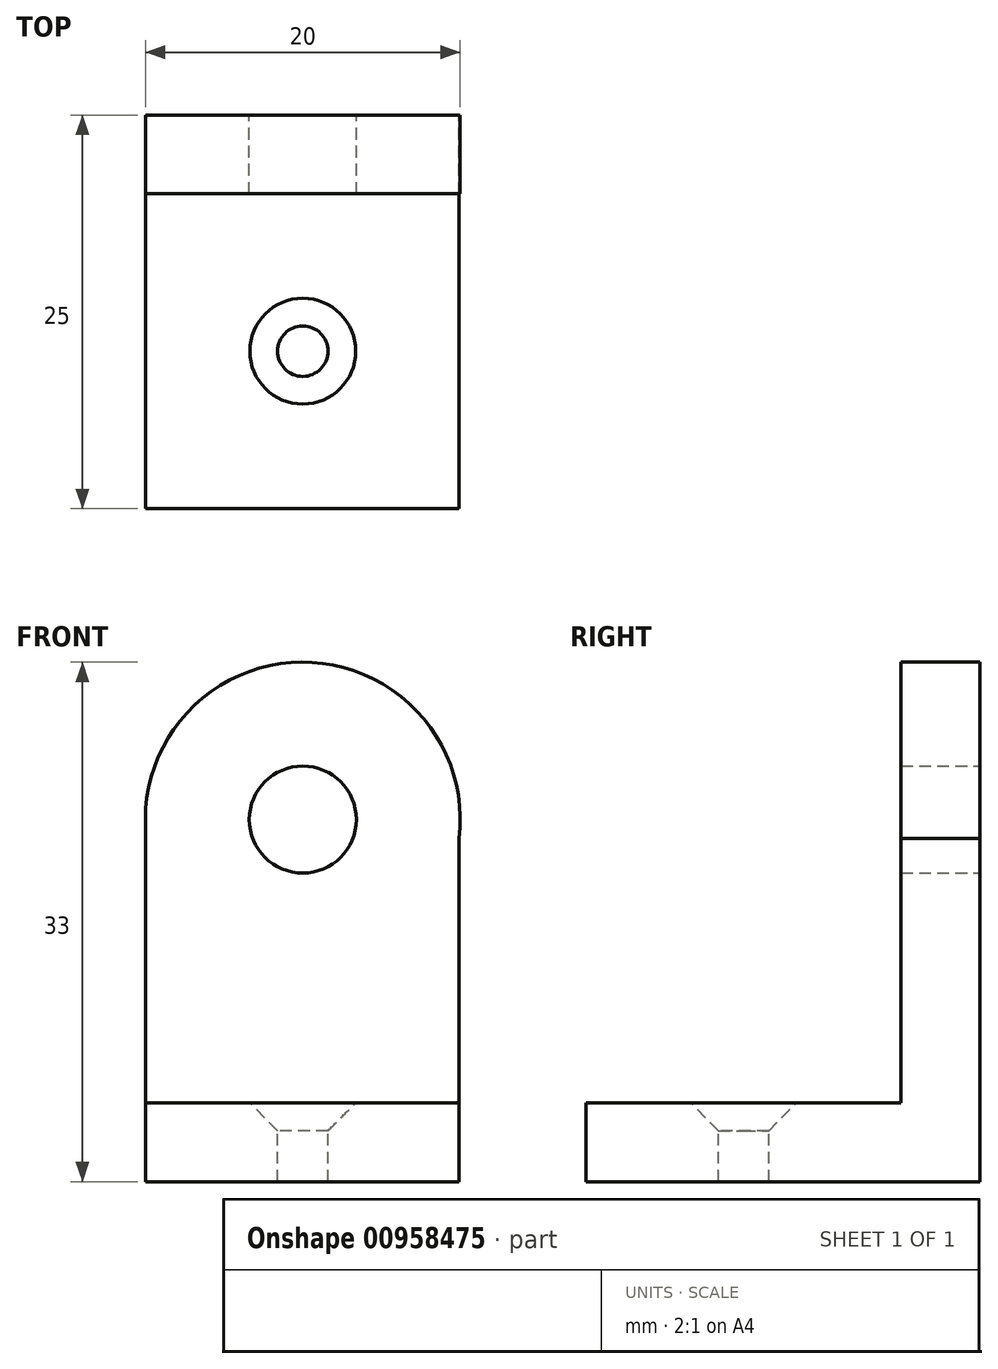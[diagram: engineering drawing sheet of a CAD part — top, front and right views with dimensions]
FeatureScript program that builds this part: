
annotation { "Feature Type Name" : "Feature", "Feature Type Description" : "" }
export const myFeature = defineFeature(function(context is Context, id is Id, definition is map)
    precondition{}
    {
        {
            var Q0;
            Q0=qCreatedBy(makeId("Front.planeOp"),FACE);
            var sketch = newSketch(context, id + "F0", { "sketchPlane" : qUnion([Q0])});
            skArc(sketch, "E0", {"start": v(9.93, -1.19) * mm, "mid": v(0.6, 9.98) * mm, "end": v(-10, 0) * mm});
            skLineSegment(sketch, "E1.top", {"start": v(-10, -23) * mm, "end": v(9.93, -23) * mm});
            skLineSegment(sketch, "E1.left", {"start": v(-10, 0) * mm, "end": v(-10, -23) * mm});
            skLineSegment(sketch, "E1.right", {"start": v(9.93, 0) * mm, "end": v(9.93, -23) * mm});
            skSolve(sketch);
        }
        {
            var Q0;
            {var subQ0=sQuery(id+"F0.wireOp",EDGE,"E0");Q0=makeQuery(id+"F0.imprint","IMPRINT",FACE,{"disambiguationData":[TD([[makeQuery(id+"F0.imprint","IMPRINT",EDGE,{"derivedFrom":subQ0}),1.0]])]});}
            extrude(context, id + "F1", {"entities" : qUnion([Q0]), "depth" : 5 * mm, "offsetDistance" : 25 * mm});
        }
        {
            var Q0;
            Q0=makeQuery(id+"F1.opExtrude","CAP_FACE",FACE,{"disambiguationData":[OSD([sQuery(id+"F0.wireOp",EDGE,"E0"),sQuery(id+"F0.wireOp",EDGE,"E1.top"),sQuery(id+"F0.wireOp",EDGE,"E1.left"),sQuery(id+"F0.wireOp",EDGE,"E1.right")])],"isStart":false});
            var sketch = newSketch(context, id + "F2", { "sketchPlane" : qUnion([Q0])});
            skLineSegment(sketch, "E2.bottom", {"start": v(-10, -23) * mm, "end": v(9.93, -23) * mm});
            skLineSegment(sketch, "E2.top", {"start": v(-10, -18) * mm, "end": v(9.93, -18) * mm});
            skLineSegment(sketch, "E2.left", {"start": v(-10, -23) * mm, "end": v(-10, -18) * mm});
            skLineSegment(sketch, "E2.right", {"start": v(9.93, -23) * mm, "end": v(9.93, -18) * mm});
            skSolve(sketch);
        }
        {
            var Q0;
            Q0=makeQuery(id+"F2.imprint","IMPRINT",FACE,{"disambiguationData":[TD([[makeQuery(id+"F2.imprint","IMPRINT",EDGE,{"derivedFrom":sQuery(id+"F2.wireOp",EDGE,"E2.bottom")}),1.0]])]});
            extrude(context, id + "F3", {"entities" : qUnion([Q0]), "operationType" : NewBodyOperationType.ADD, "depth" : 20 * mm, "offsetDistance" : 25 * mm});
        }
        {
            var Q0;
            Q0=makeQuery(id+"F1.opExtrude","CAP_FACE",FACE,{"disambiguationData":[OSD([sQuery(id+"F0.wireOp",EDGE,"E0"),sQuery(id+"F0.wireOp",EDGE,"E1.top"),sQuery(id+"F0.wireOp",EDGE,"E1.left"),sQuery(id+"F0.wireOp",EDGE,"E1.right")])],"isStart":true});
            var sketch = newSketch(context, id + "F4", { "sketchPlane" : qUnion([Q0])});
            skPoint(sketch, "E3", {"position": v(0, 0) * mm});
            skSolve(sketch);
        }
        {
            var Q0;
            Q0=sQuery(id+"F4.wireOp",VERTEX,"E3");
            var Q1;
            Q1=makeQuery(id+"F1.opExtrude","SWEPT_BODY",BODY,{"disambiguationData":[OSD([sQuery(id+"F0.wireOp",EDGE,"E0"),sQuery(id+"F0.wireOp",EDGE,"E1.top"),sQuery(id+"F0.wireOp",EDGE,"E1.left"),sQuery(id+"F0.wireOp",EDGE,"E1.right")])]});
            hole(context, id + "F5", {"style" : HoleStyle.SIMPLE, "endStyle" : HoleEndStyle.THROUGH, "standardTappedOrClearance" : lookupTablePath({ "standard" : "ISO", "engagement" : "75%", "pitch" : "1.25 mm", "size" : "M8", "type" : "Tapped" }), "standardBlindInLast" : lookupTablePath({ "standard" : "ISO", "fit" : "Normal", "engagement" : "75%", "pitch" : "1.25 mm", "size" : "M8", "type" : "Clearance & tapped" }), "holeDiameter" : 6.8 * mm, "majorDiameter" : 8 * mm, "showTappedDepth" : true, "isTappedThrough" : true, "tappedDepth" : 12 * mm, "tapClearance" : 3, "locations" : qUnion([Q0]), "scope" : qUnion([Q1])});
        }
        {
            var Q0;
            Q0=makeQuery(id+"F3.opExtrude","SWEPT_FACE",FACE,{"disambiguationData":[OSD([sQuery(id+"F2.wireOp",EDGE,"E2.top")])]});
            var sketch = newSketch(context, id + "F6", { "sketchPlane" : qUnion([Q0])});
            skPoint(sketch, "E4", {"position": v(0, -15) * mm});
            skSolve(sketch);
        }
        {
            var Q0;
            Q0=sQuery(id+"F6.wireOp",VERTEX,"E4");
            var Q1;
            Q1=makeQuery(id+"F1.opExtrude","SWEPT_BODY",BODY,{"disambiguationData":[OSD([sQuery(id+"F0.wireOp",EDGE,"E0"),sQuery(id+"F0.wireOp",EDGE,"E1.top"),sQuery(id+"F0.wireOp",EDGE,"E1.left"),sQuery(id+"F0.wireOp",EDGE,"E1.right")])]});
            hole(context, id + "F7", {"style" : HoleStyle.C_SINK, "endStyle" : HoleEndStyle.THROUGH, "standardTappedOrClearance" : lookupTablePath({ "fit" : "Close", "standard" : "ISO", "size" : "M3", "type" : "Clearance" }), "standardBlindInLast" : lookupTablePath({ "fit" : "Close", "standard" : "ISO", "engagement" : "75%", "pitch" : "0.5 mm", "size" : "M3", "type" : "Clearance & tapped" }), "holeDiameter" : 3.2 * mm, "cSinkDiameter" : 6.72 * mm, "cSinkAngle" : 90 * degree, "majorDiameter" : 5 * mm, "isTappedThrough" : true, "tappedDepth" : 12 * mm, "tapClearance" : 3, "locations" : qUnion([Q0]), "scope" : qUnion([Q1])});
        }
    });
